# Revit family: QF_ELECTROLUXPROFESSIONAL_1LSNJ8_IC64821LF_S
name_source: partatom
category: Attrezzature speciali
units: mm (PartAtom-declared; Revit-internal decimal feet)

## family parameters
Basato su piano di lavoro = No
Condiviso = No
Punto di calcolo locali = No
Quota connettore circolare = Usa diametro
Sempre verticale = Sì
Taglio con vuoti quando caricato = No
Tipo di parte = Normale

## types (2) — shared parameters
Cycle = 50 Hz
Depth Actual = 1110 mm  [stored 3.64173 ft]
Height Actual = 1270 mm  [stored 4.16667 ft]
Latent Heat Output = 0.0
Length Actual = 2775 mm  [stored 9.10433 ft]
Modello = IC64821LF
Phase = 3
Produttore = Electrolux Professional
Sensible Heat Output = 0.0
Steam Pounds per Hour = 92
URL = www.electroluxprofessional.com
Volts = 400 V
Watts = 1400 W
Weight = 810
zero-valued in all types: Gas KW, Prospetto di default

## per-type parameters (varying)
| type | Descrizione | Item Number |
| 9882030302 | IRONER CYLINDER IC64821LF LENGTH FOLDING 2120MM STEAM CE 400/50/3 4MM SST CYL. SE, DK, FI VAC.FEED.TABLE ANTISTATIC DIAM | 1LT66Y |
| 9882030282 | IRONER CYLINDER IC64821LF LENGTH FOLDING 2120MM SUPERIOR STEAM CE 400/50/3 4MM SST CYL. FR FEED ALONE VAC.FEED.TABLE ANT | 1L0H52 |

note: [stored X ft] marks values corroborated as IEEE doubles in the binary element streams (Revit-internal decimal feet)

## geometry (parser evidence)
native form markers: Sweep x11
no freeform markers — native parametric forms only
